# Revit family: ARGON-PLAF_IP65_40W_PC_OPAL+_CONNECT_RAPIDES_1200MM
name_source: partatom
category: Lighting Fixtures
units: mm (PartAtom-declared; Revit-internal decimal feet)

## family parameters
Always vertical = Yes
Cut with Voids When Loaded = No
Host = Ceiling
Light Source = Yes
OmniClass Number = 23.80.70.11
OmniClass Title = Luminaries for Internal Lighting
Part Type = Normal
Room Calculation Point = No
Round Connector Dimension = Use Diameter
Shared = No

## types (1)
- ARGON-PLAF_IP65_40W_PC_OPAL+_CONNECT_RAPIDES_1200MM
    Alimentation Driver = AC 220-240V
    Alimentation luminaire = 510mA/60-80V dc
    Color Filter = 16777215
    Default Elevation = 0 mm  [stored 0 ft]
    Diffuseur = Polycarbonate opale
    Dimensions = 1140 x 75 x 66 mm
    Dimming Lamp Color Temperature Shift = <None>
    Driver = Driver OEM
    Durée de vie = 50 000 heures
    Emit from Line Length = 609.6 mm  [stored 2 ft]
    IRC = 80
    Lamp = LED SMD 2835
    Maintien du flux = L80B10 (50 000 heures)
    Manufacturer = Lucera - Lucera (c) 06/01/2021 16:38:18 +01:00
    Matériau = ABS
    Photometric Web File = google_eulumdat_converter.ies
    Puissance nominale = 40W
    Tilt Angle = 90.00°
    URL = https://www.lucera.fr
    Wattage Comments = 40W

note: [stored X ft] marks values corroborated as IEEE doubles in the binary element streams (Revit-internal decimal feet)

## geometry (parser evidence)
native form markers: Sweep x2
no freeform markers — native parametric forms only
